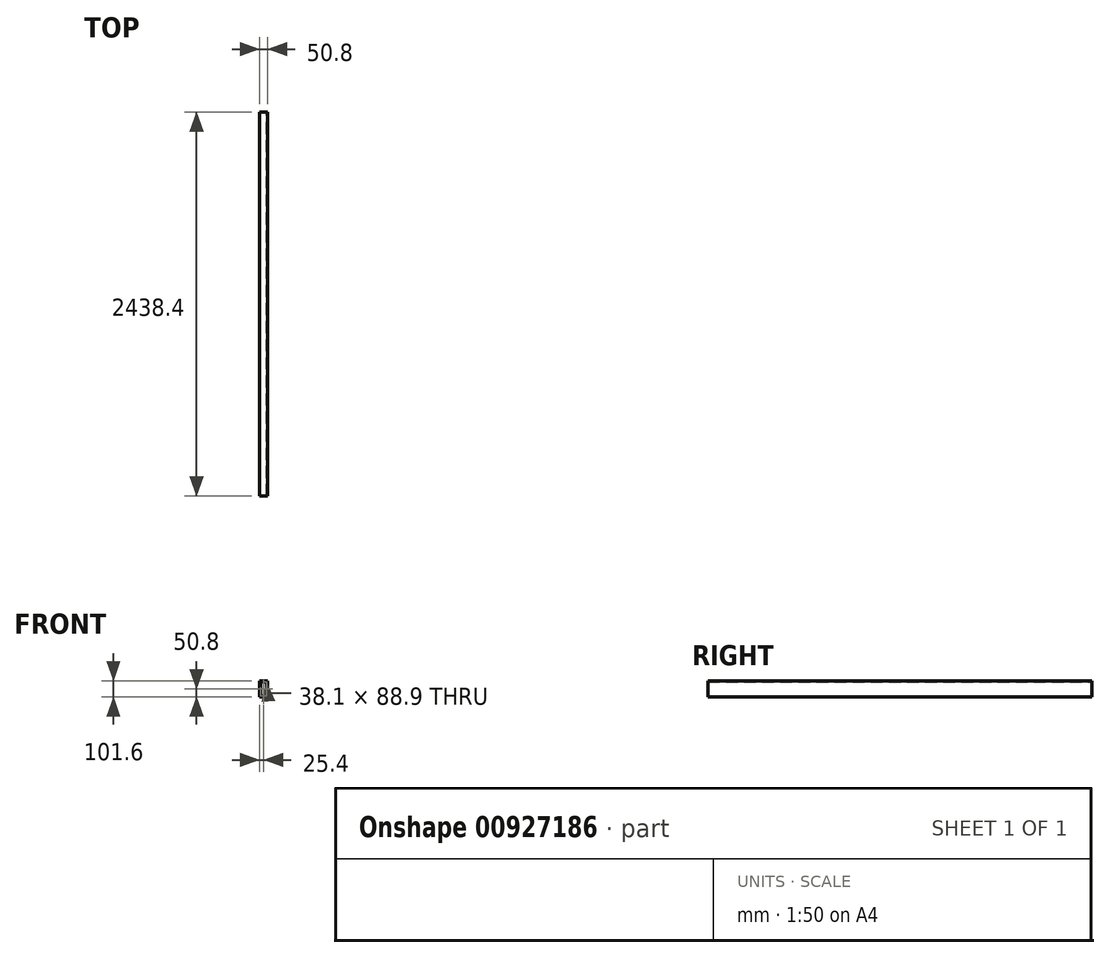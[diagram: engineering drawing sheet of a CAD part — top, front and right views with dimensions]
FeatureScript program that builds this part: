
annotation { "Feature Type Name" : "Feature", "Feature Type Description" : "" }
export const myFeature = defineFeature(function(context is Context, id is Id, definition is map)
    precondition{}
    {
        {
            var Q0;
            Q0=qCreatedBy(makeId("Front.planeOp"),FACE);
            var sketch = newSketch(context, id + "F0", { "sketchPlane" : qUnion([Q0])});
            skLineSegment(sketch, "E0.bottom", {"start": v(25.4, 50.8) * mm, "end": v(-25.4, 50.8) * mm});
            skLineSegment(sketch, "E0.top", {"start": v(25.4, -50.8) * mm, "end": v(-25.4, -50.8) * mm});
            skLineSegment(sketch, "E0.left", {"start": v(25.4, 50.8) * mm, "end": v(25.4, -50.8) * mm});
            skLineSegment(sketch, "E0.right", {"start": v(-25.4, 50.8) * mm, "end": v(-25.4, -50.8) * mm});
            skPoint(sketch, "E0.middle", {"position": v(0, 0) * mm});
            skLineSegment(sketch, "E1.0", {"start": v(19.05, 44.45) * mm, "end": v(-19.05, 44.45) * mm});
            skLineSegment(sketch, "E1.1", {"start": v(19.05, 44.45) * mm, "end": v(19.05, -44.45) * mm});
            skLineSegment(sketch, "E1.2", {"start": v(19.05, -44.45) * mm, "end": v(-19.05, -44.45) * mm});
            skLineSegment(sketch, "E1.3", {"start": v(-19.05, 44.45) * mm, "end": v(-19.05, -44.45) * mm});
            skSolve(sketch);
        }
        {
            var Q0;
            Q0=makeQuery(id+"F0.imprint","IMPRINT",FACE,{"disambiguationData":[TD([[makeQuery(id+"F0.imprint","IMPRINT",EDGE,{"derivedFrom":sQuery(id+"F0.wireOp",EDGE,"E0.bottom")}),1.0]])]});
            extrude(context, id + "F1", {"entities" : qUnion([Q0]), "endBound" : BoundingType.SYMMETRIC, "depth" : 2438.4 * mm, "offsetDistance" : 25.4 * mm});
        }
    });
